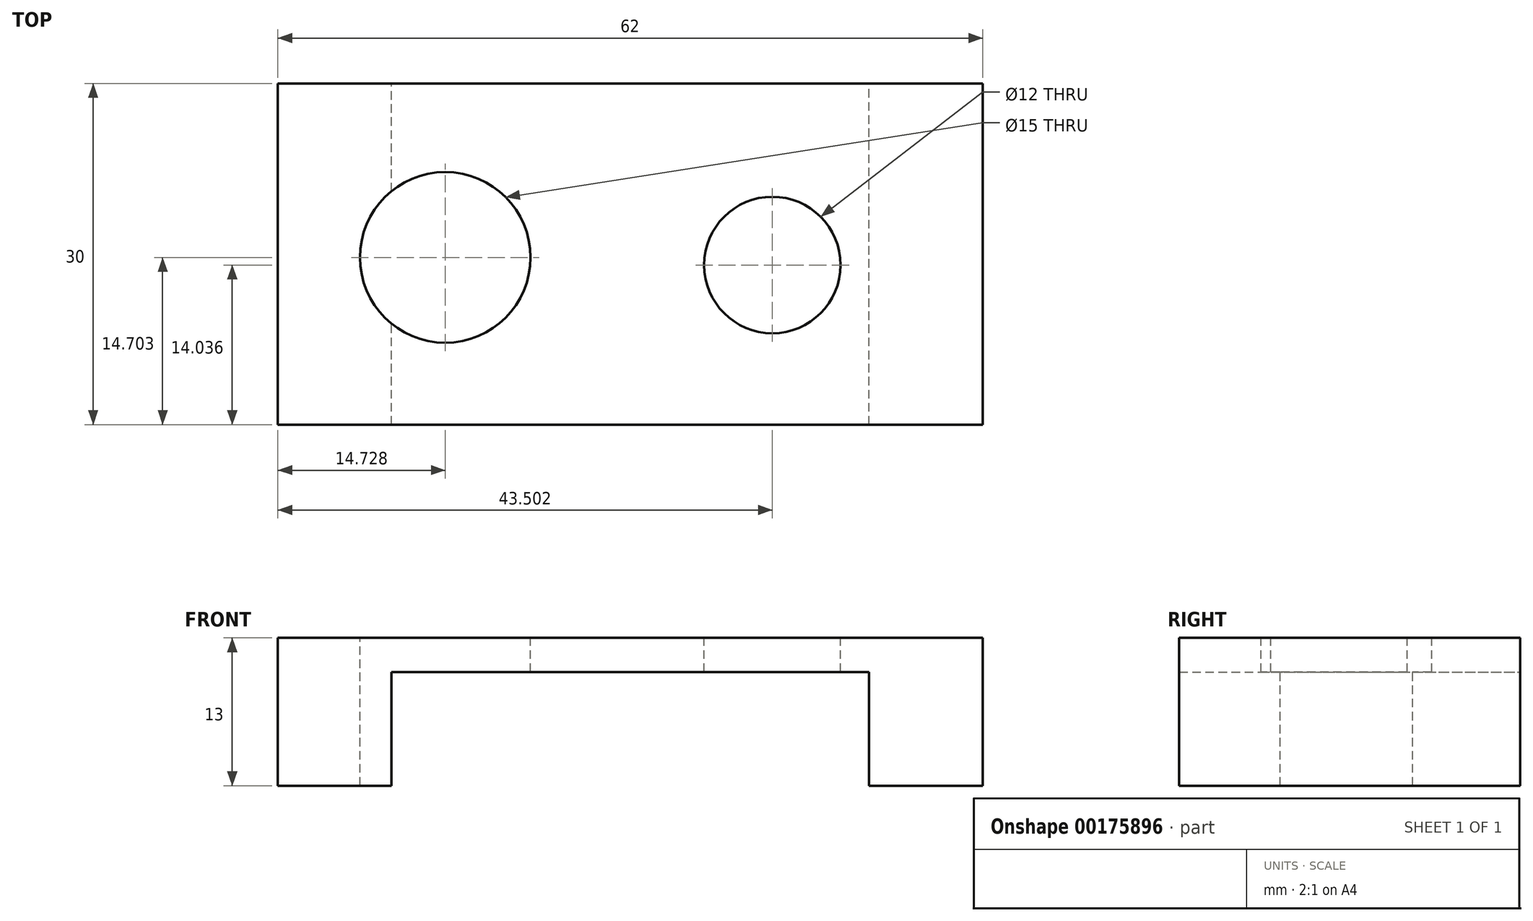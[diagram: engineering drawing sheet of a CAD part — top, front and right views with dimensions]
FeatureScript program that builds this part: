
annotation { "Feature Type Name" : "Feature", "Feature Type Description" : "" }
export const myFeature = defineFeature(function(context is Context, id is Id, definition is map)
    precondition{}
    {
        {
            var Q0;
            Q0=qCreatedBy(makeId("Front.planeOp"),FACE);
            var sketch = newSketch(context, id + "F0", { "sketchPlane" : qUnion([Q0])});
            skLineSegment(sketch, "E0", {"start": v(0, -13) * mm, "end": v(10, -13) * mm});
            skLineSegment(sketch, "E1", {"start": v(10, -13) * mm, "end": v(10, -3) * mm});
            skLineSegment(sketch, "E2", {"start": v(10, -3) * mm, "end": v(52, -3) * mm});
            skLineSegment(sketch, "E3", {"start": v(52, -3) * mm, "end": v(52, -13) * mm});
            skLineSegment(sketch, "E4", {"start": v(52, -13) * mm, "end": v(62, -13) * mm});
            skLineSegment(sketch, "E5", {"start": v(62, -13) * mm, "end": v(62, 0) * mm});
            skLineSegment(sketch, "E6", {"start": v(62, 0) * mm, "end": v(0, 0) * mm});
            skLineSegment(sketch, "E7", {"start": v(0, 0) * mm, "end": v(0, -13) * mm});
            skSolve(sketch);
        }
        {
            var Q0;
            Q0=makeQuery(id+"F0.imprint","IMPRINT",FACE,{"disambiguationData":[TD([[makeQuery(id+"F0.imprint","IMPRINT",EDGE,{"derivedFrom":sQuery(id+"F0.wireOp",EDGE,"E0")}),1.0]])]});
            var sketch = newSketch(context, id + "F1", { "sketchPlane" : qUnion([Q0])});
            skSolve(sketch);
        }
        {
            var Q0;
            Q0=makeQuery(id+"F0.imprint","IMPRINT",FACE,{"disambiguationData":[TD([[makeQuery(id+"F0.imprint","IMPRINT",EDGE,{"derivedFrom":sQuery(id+"F0.wireOp",EDGE,"E0")}),1.0]])]});
            extrude(context, id + "F2", {"entities" : qUnion([Q0]), "depth" : 30 * mm});
        }
        {
            var Q0;
            Q0=makeQuery(id+"F1.imprint","IMPRINT",FACE,{"disambiguationData":[TD([[makeQuery(id+"F1.imprint","IMPRINT",EDGE,{"derivedFrom":makeQuery(id+"F0.imprint","IMPRINT",EDGE,{"derivedFrom":sQuery(id+"F0.wireOp",EDGE,"E0")})}),1.0]])]});
            extrude(context, id + "F3", {"entities" : qUnion([Q0]), "operationType" : NewBodyOperationType.ADD, "depth" : 30 * mm});
        }
        {
            var Q0;
            Q0=makeQuery(id+"F2.opExtrude","SWEPT_FACE",FACE,{"disambiguationData":[OSD([sQuery(id+"F0.wireOp",EDGE,"E6")])]});
            var sketch = newSketch(context, id + "F4", { "sketchPlane" : qUnion([Q0])});
            skCircle(sketch, "E8", {"center": v(14.73, -15.3) * mm, "radius": 7.5 * mm});
            skCircle(sketch, "E9", {"center": v(43.5, -15.96) * mm, "radius": 6 * mm});
            skSolve(sketch);
        }
        {
            var Q0;
            Q0=makeQuery(id+"F4.imprint","IMPRINT",FACE,{"disambiguationData":[TD([[makeQuery(id+"F4.imprint","IMPRINT",EDGE,{"derivedFrom":sQuery(id+"F4.wireOp",EDGE,"E8")}),1.0]])]});
            var Q1;
            Q1=makeQuery(id+"F4.imprint","IMPRINT",FACE,{"disambiguationData":[TD([[makeQuery(id+"F4.imprint","IMPRINT",EDGE,{"derivedFrom":sQuery(id+"F4.wireOp",EDGE,"E9")}),1.0]])]});
            extrude(context, id + "F5", {"entities" : qUnion([Q0, Q1]), "operationType" : NewBodyOperationType.REMOVE, "oppositeDirection" : true, "depth" : 25 * mm});
        }
    });
